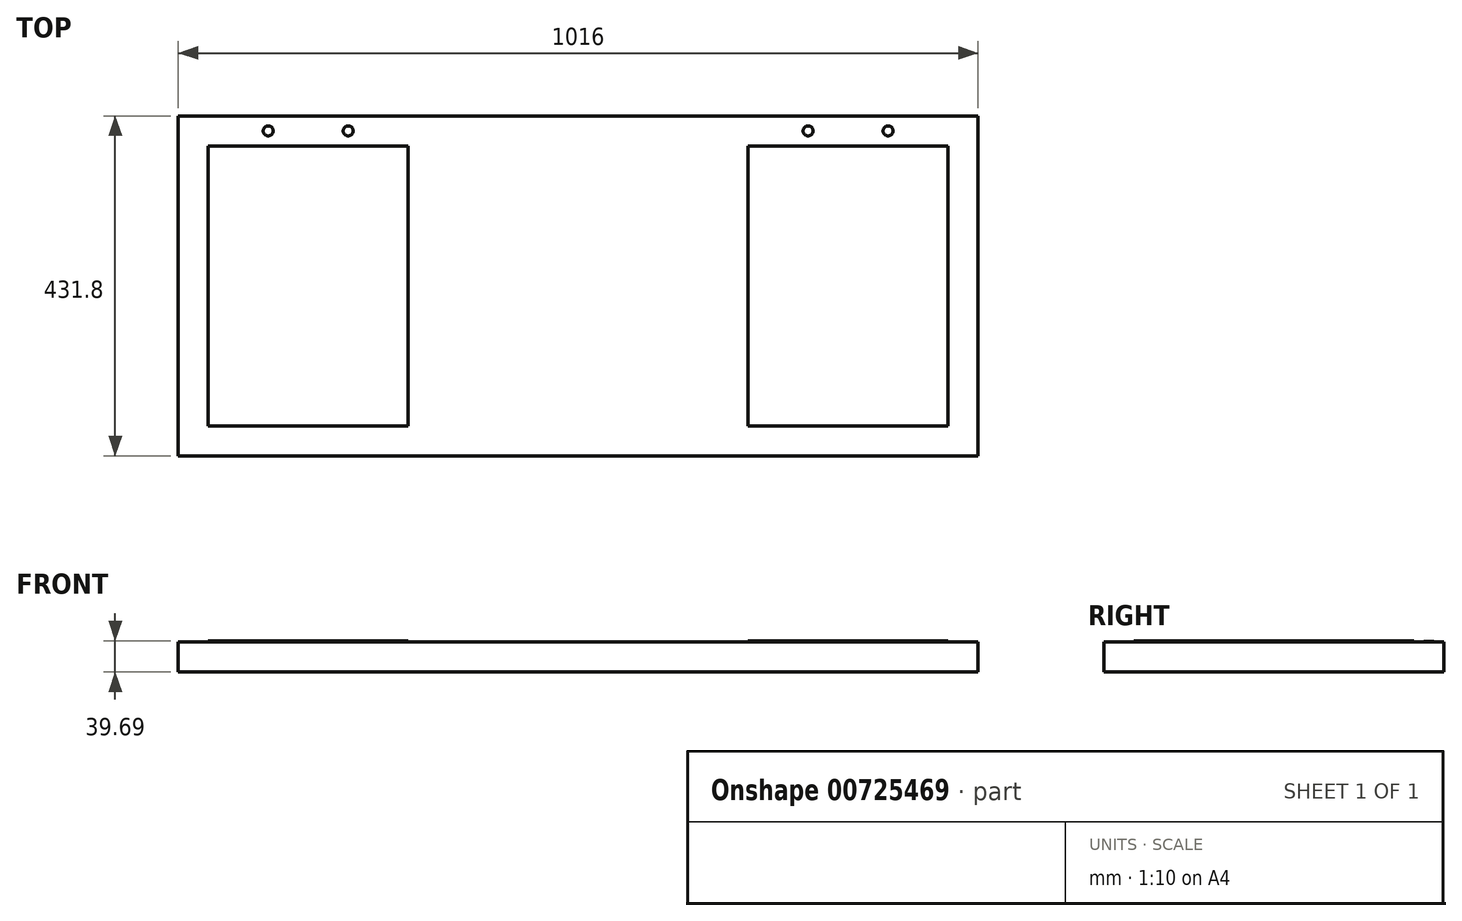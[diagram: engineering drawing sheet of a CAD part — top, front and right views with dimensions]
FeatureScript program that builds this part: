
annotation { "Feature Type Name" : "Feature", "Feature Type Description" : "" }
export const myFeature = defineFeature(function(context is Context, id is Id, definition is map)
    precondition{}
    {
        {
            var Q0;
            Q0=qCreatedBy(makeId("Top.planeOp"),FACE);
            var sketch = newSketch(context, id + "F0", { "sketchPlane" : qUnion([Q0])});
            skLineSegment(sketch, "E0.bottom", {"start": v(-507.23, 223.88) * mm, "end": v(508.77, 223.88) * mm});
            skLineSegment(sketch, "E0.top", {"start": v(-507.23, -207.92) * mm, "end": v(508.77, -207.92) * mm});
            skLineSegment(sketch, "E0.left", {"start": v(-507.23, 223.88) * mm, "end": v(-507.23, -207.92) * mm});
            skLineSegment(sketch, "E0.right", {"start": v(508.77, 223.88) * mm, "end": v(508.77, -207.92) * mm});
            skLineSegment(sketch, "E1.bottom", {"start": v(-469.13, 185.78) * mm, "end": v(-215.13, 185.78) * mm});
            skLineSegment(sketch, "E1.top", {"start": v(-469.13, -169.82) * mm, "end": v(-215.13, -169.82) * mm});
            skLineSegment(sketch, "E1.left", {"start": v(-469.13, 185.78) * mm, "end": v(-469.13, -169.82) * mm});
            skLineSegment(sketch, "E1.right", {"start": v(-215.13, 185.78) * mm, "end": v(-215.13, -169.82) * mm});
            skLineSegment(sketch, "E2.bottom", {"start": v(470.67, 185.78) * mm, "end": v(216.67, 185.78) * mm});
            skLineSegment(sketch, "E2.top", {"start": v(470.67, -169.82) * mm, "end": v(216.67, -169.82) * mm});
            skLineSegment(sketch, "E2.left", {"start": v(470.67, 185.78) * mm, "end": v(470.67, -169.82) * mm});
            skLineSegment(sketch, "E2.right", {"start": v(216.67, 185.78) * mm, "end": v(216.67, -169.82) * mm});
            skCircle(sketch, "E3", {"center": v(292.87, 204.83) * mm, "radius": 6.35 * mm});
            skCircle(sketch, "E4", {"center": v(394.47, 204.83) * mm, "radius": 6.35 * mm});
            skCircle(sketch, "E5", {"center": v(-392.93, 204.83) * mm, "radius": 6.35 * mm});
            skCircle(sketch, "E6", {"center": v(-291.33, 204.83) * mm, "radius": 6.35 * mm});
            skSolve(sketch);
        }
        {
            var Q0;
            Q0=makeQuery(id+"F0.imprint","IMPRINT",FACE,{"disambiguationData":[TD([[makeQuery(id+"F0.imprint","IMPRINT",EDGE,{"derivedFrom":sQuery(id+"F0.wireOp",EDGE,"E0.bottom")}),-1.0]])]});
            var Q1;
            Q1=makeQuery(id+"F0.imprint","IMPRINT",FACE,{"disambiguationData":[TD([[makeQuery(id+"F0.imprint","IMPRINT",EDGE,{"derivedFrom":sQuery(id+"F0.wireOp",EDGE,"E1.bottom")}),-1.0]])]});
            var Q2;
            Q2=makeQuery(id+"F0.imprint","IMPRINT",FACE,{"disambiguationData":[TD([[makeQuery(id+"F0.imprint","IMPRINT",EDGE,{"derivedFrom":sQuery(id+"F0.wireOp",EDGE,"E2.bottom")}),1.0]])]});
            var Q3;
            Q3=makeQuery(id+"F0.imprint","IMPRINT",FACE,{"disambiguationData":[TD([[makeQuery(id+"F0.imprint","IMPRINT",EDGE,{"derivedFrom":sQuery(id+"F0.wireOp",EDGE,"E3")}),1.0]])]});
            var Q4;
            Q4=makeQuery(id+"F0.imprint","IMPRINT",FACE,{"disambiguationData":[TD([[makeQuery(id+"F0.imprint","IMPRINT",EDGE,{"derivedFrom":sQuery(id+"F0.wireOp",EDGE,"E4")}),1.0]])]});
            var Q5;
            Q5=makeQuery(id+"F0.imprint","IMPRINT",FACE,{"disambiguationData":[TD([[makeQuery(id+"F0.imprint","IMPRINT",EDGE,{"derivedFrom":sQuery(id+"F0.wireOp",EDGE,"E6")}),1.0]])]});
            var Q6;
            Q6=makeQuery(id+"F0.imprint","IMPRINT",FACE,{"disambiguationData":[TD([[makeQuery(id+"F0.imprint","IMPRINT",EDGE,{"derivedFrom":sQuery(id+"F0.wireOp",EDGE,"E5")}),1.0]])]});
            extrude(context, id + "F1", {"entities" : qUnion([Q0, Q1, Q2, Q3, Q4, Q5, Q6]), "oppositeDirection" : true, "depth" : 38.1 * mm, "offsetDistance" : 25.4 * mm});
        }
        {
            var Q0;
            Q0=makeQuery(id+"F0.imprint","IMPRINT",FACE,{"disambiguationData":[TD([[makeQuery(id+"F0.imprint","IMPRINT",EDGE,{"derivedFrom":sQuery(id+"F0.wireOp",EDGE,"E1.bottom")}),-1.0]])]});
            var Q1;
            Q1=makeQuery(id+"F0.imprint","IMPRINT",FACE,{"disambiguationData":[TD([[makeQuery(id+"F0.imprint","IMPRINT",EDGE,{"derivedFrom":sQuery(id+"F0.wireOp",EDGE,"E2.bottom")}),1.0]])]});
            extrude(context, id + "F2", {"entities" : qUnion([Q0, Q1]), "operationType" : NewBodyOperationType.ADD, "depth" : 1.59 * mm, "offsetDistance" : 25.4 * mm});
        }
        {
            var Q0;
            Q0=makeQuery(id+"F0.imprint","IMPRINT",FACE,{"disambiguationData":[TD([[makeQuery(id+"F0.imprint","IMPRINT",EDGE,{"derivedFrom":sQuery(id+"F0.wireOp",EDGE,"E3")}),1.0]])]});
            var Q1;
            Q1=makeQuery(id+"F0.imprint","IMPRINT",FACE,{"disambiguationData":[TD([[makeQuery(id+"F0.imprint","IMPRINT",EDGE,{"derivedFrom":sQuery(id+"F0.wireOp",EDGE,"E4")}),1.0]])]});
            var Q2;
            Q2=makeQuery(id+"F0.imprint","IMPRINT",FACE,{"disambiguationData":[TD([[makeQuery(id+"F0.imprint","IMPRINT",EDGE,{"derivedFrom":sQuery(id+"F0.wireOp",EDGE,"E5")}),1.0]])]});
            var Q3;
            Q3=makeQuery(id+"F0.imprint","IMPRINT",FACE,{"disambiguationData":[TD([[makeQuery(id+"F0.imprint","IMPRINT",EDGE,{"derivedFrom":sQuery(id+"F0.wireOp",EDGE,"E6")}),1.0]])]});
            var Q4;
            Q4=sQuery(id+"F0.wireOp",EDGE,"E3");
            var Q5;
            Q5=sQuery(id+"F0.wireOp",EDGE,"E4");
            extrude(context, id + "F3", {"entities" : qUnion([Q0, Q1, Q2, Q3]), "operationType" : NewBodyOperationType.ADD, "surfaceOperationType" : NewSurfaceOperationType.ADD, "surfaceEntities" : qUnion([Q4, Q5]), "depth" : (1 + (1 / 16)) * mm, "offsetDistance" : 25.4 * mm});
        }
    });
